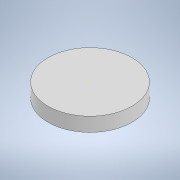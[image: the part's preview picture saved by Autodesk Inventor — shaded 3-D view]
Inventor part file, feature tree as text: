
AUTODESK INVENTOR PART (.ipt)
format: ipt  version: 2022 (Build 260153000, 153)  size: 92,672 bytes
history: native  units: mm
features: sketch x2, extrude x1
ambient origin geometry x8: Origin, YZ Plane, XZ Plane, XY Plane, X Axis, Y Axis, Z Axis, Center Point
bodies: Solid1 (feature_tree)
feature tree (3):
  extrude  "Extrusion1"  Depth=5.0mm TaperAngle=0.0deg
  sketch  "Sketch2"
  sketch  "Sketch1"  dims[d1=30.0mm d2=5.0mm d3=0.0mm]
